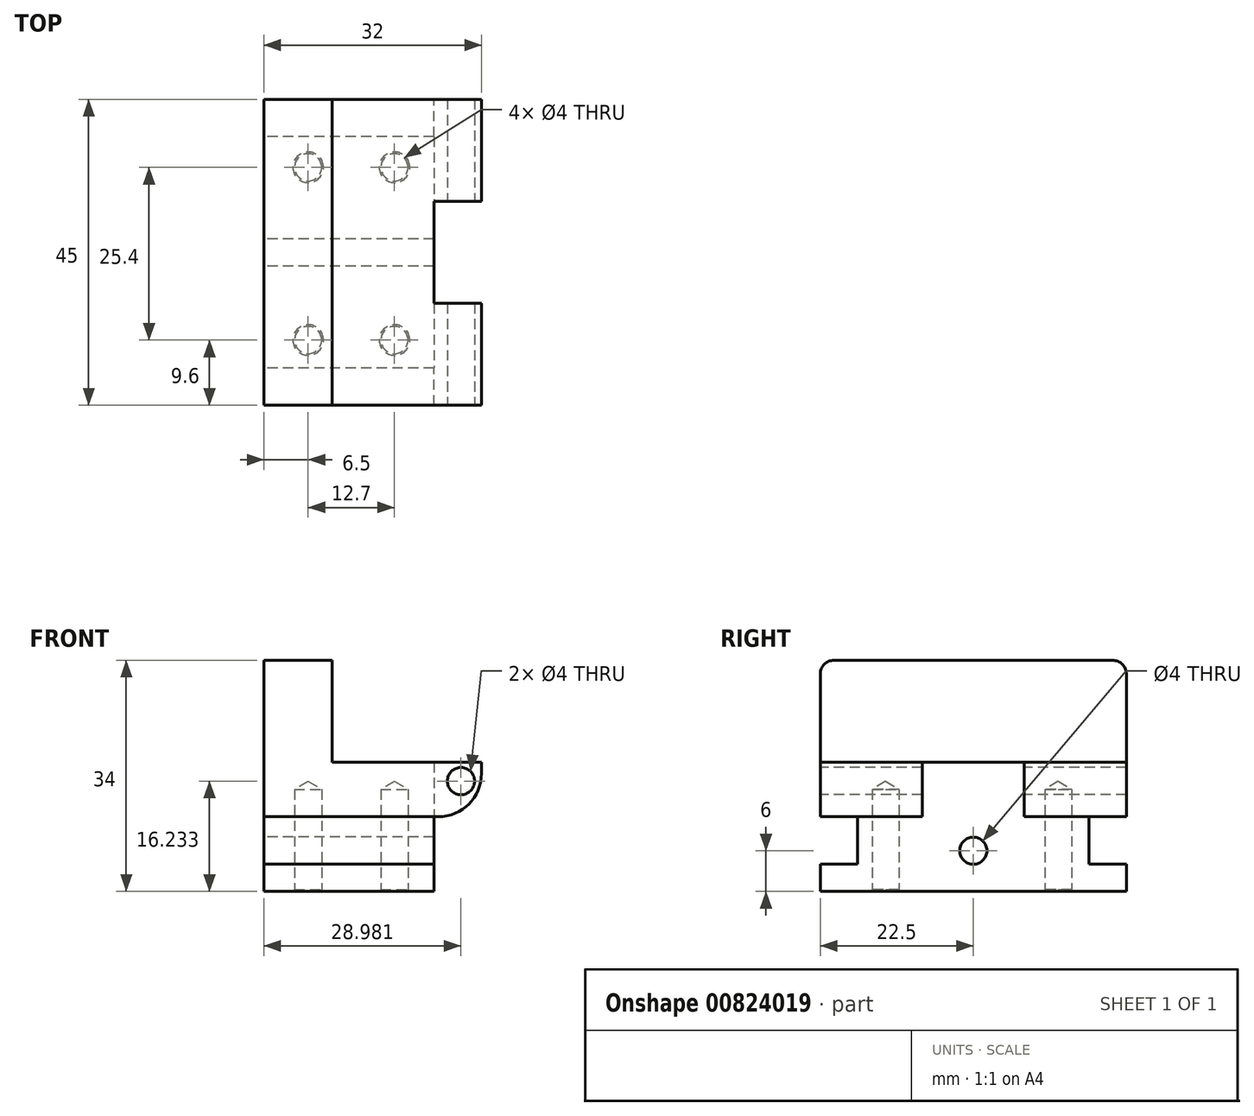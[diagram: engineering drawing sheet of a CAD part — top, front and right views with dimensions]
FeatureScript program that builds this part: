
annotation { "Feature Type Name" : "Feature", "Feature Type Description" : "" }
export const myFeature = defineFeature(function(context is Context, id is Id, definition is map)
    precondition{}
    {
        {
            var Q0;
            Q0=qCreatedBy(makeId("Right.planeOp"),FACE);
            var sketch = newSketch(context, id + "F0", { "sketchPlane" : qUnion([Q0])});
            skLineSegment(sketch, "E0.bottom", {"start": v(0, 0) * mm, "end": v(45, 0) * mm});
            skLineSegment(sketch, "E0.top", {"start": v(0, 34) * mm, "end": v(45, 34) * mm});
            skLineSegment(sketch, "E0.left", {"start": v(0, 0) * mm, "end": v(0, 4) * mm});
            skLineSegment(sketch, "E0.right", {"start": v(45, 0) * mm, "end": v(45, 4) * mm});
            skLineSegment(sketch, "E1", {"start": v(0, 4) * mm, "end": v(5.5, 4) * mm});
            skLineSegment(sketch, "E2", {"start": v(0, 11) * mm, "end": v(5.5, 11) * mm});
            skLineSegment(sketch, "E3", {"start": v(5.5, 11) * mm, "end": v(5.5, 4) * mm});
            skLineSegment(sketch, "E4", {"start": v(39.5, 11) * mm, "end": v(39.5, 4) * mm});
            skLineSegment(sketch, "E5.trimOffspring", {"start": v(39.5, 11) * mm, "end": v(45, 11) * mm});
            skLineSegment(sketch, "E6.trimOffspring", {"start": v(39.5, 4) * mm, "end": v(45, 4) * mm});
            skLineSegment(sketch, "E7.trimOffspring", {"start": v(0, 11) * mm, "end": v(0, 34) * mm});
            skLineSegment(sketch, "E8.trimOffspring", {"start": v(45, 11) * mm, "end": v(45, 34) * mm});
            skSolve(sketch);
        }
        {
            var Q0;
            Q0 = qSketchRegion(id + "F0", true);
            extrude(context, id + "F1", {"entities" : qUnion([Q0]), "depth" : 25 * mm, "offsetDistance" : 25.4 * mm});
        }
        {
            var Q0;
            Q0=makeQuery(id+"F1.opExtrude","SWEPT_FACE",FACE,{"disambiguationData":[OSD([sQuery(id+"F0.wireOp",EDGE,"E7.trimOffspring")])]});
            var sketch = newSketch(context, id + "F2", { "sketchPlane" : qUnion([Q0])});
            skLineSegment(sketch, "E9", {"start": v(10, 34) * mm, "end": v(10, 19) * mm});
            skLineSegment(sketch, "E10", {"start": v(10, 19) * mm, "end": v(25, 19) * mm});
            skLineSegment(sketch, "E11", {"start": v(25, 19) * mm, "end": v(25, 34) * mm});
            skLineSegment(sketch, "E12", {"start": v(25, 34) * mm, "end": v(10, 34) * mm});
            skSolve(sketch);
        }
        {
            var Q0;
            Q0=makeQuery(id+"F2.imprint","IMPRINT",FACE,{"disambiguationData":[TD([[makeQuery(id+"F2.imprint","IMPRINT",EDGE,{"derivedFrom":sQuery(id+"F2.wireOp",EDGE,"E9")}),1.0]])]});
            extrude(context, id + "F3", {"entities" : qUnion([Q0]), "operationType" : NewBodyOperationType.REMOVE, "endBound" : BoundingType.UP_TO_NEXT, "oppositeDirection" : true, "depth" : 25.4 * mm, "offsetDistance" : 25.4 * mm});
        }
        {
            var Q0;
            Q0=makeQuery(id+"F3.boolean.opBoolean","COPY",EDGE,{"derivedFrom":makeQuery(id+"F3.opExtrude","SWEPT_EDGE",EDGE,{"disambiguationData":[OSD([sQuery(id+"F0.wireOp",EDGE,"E0.top"),sQuery(id+"F0.wireOp",EDGE,"E7.trimOffspring"),sQuery(id+"F2.wireOp",EDGE,"E9"),sQuery(id+"F2.wireOp",EDGE,"E12")])]})});
            var Q1;
            Q1=makeQuery(id+"F1.opExtrude","SWEPT_EDGE",EDGE,{"disambiguationData":[OSD([sQuery(id+"F0.wireOp",EDGE,"E0.top"),sQuery(id+"F0.wireOp",EDGE,"E7.trimOffspring")])]});
            var Q2;
            Q2=makeQuery(id+"F1.opExtrude","SWEPT_EDGE",EDGE,{"disambiguationData":[OSD([sQuery(id+"F0.wireOp",EDGE,"E0.top"),sQuery(id+"F0.wireOp",EDGE,"E8.trimOffspring")])]});
            fillet(context, id + "F4", {"entities" : qUnion([Q0, Q1, Q2]), "radius" : 2 * mm, "tangentPropagation" : true, "allowEdgeOverflow" : false});
        }
        {
            var Q0;
            Q0=makeQuery(id+"F1.opExtrude","CAP_FACE",FACE,{"disambiguationData":[OSD([sQuery(id+"F0.wireOp",EDGE,"E0.bottom"),sQuery(id+"F0.wireOp",EDGE,"E0.top"),sQuery(id+"F0.wireOp",EDGE,"E0.left"),sQuery(id+"F0.wireOp",EDGE,"E0.right"),sQuery(id+"F0.wireOp",EDGE,"E1"),sQuery(id+"F0.wireOp",EDGE,"E2"),sQuery(id+"F0.wireOp",EDGE,"E3"),sQuery(id+"F0.wireOp",EDGE,"E4"),sQuery(id+"F0.wireOp",EDGE,"E5.trimOffspring"),sQuery(id+"F0.wireOp",EDGE,"E6.trimOffspring"),sQuery(id+"F0.wireOp",EDGE,"E7.trimOffspring"),sQuery(id+"F0.wireOp",EDGE,"E8.trimOffspring")])],"isStart":true});
            var sketch = newSketch(context, id + "F5", { "sketchPlane" : qUnion([Q0])});
            skPoint(sketch, "E13", {"position": v(-22.5, 6) * mm});
            skSolve(sketch);
        }
        {
            var Q0;
            Q0=sQuery(id+"F5.wireOp",VERTEX,"E13");
            var Q1;
            Q1=makeQuery(id+"F1.opExtrude","SWEPT_BODY",BODY,{"disambiguationData":[OSD([sQuery(id+"F0.wireOp",EDGE,"E0.bottom"),sQuery(id+"F0.wireOp",EDGE,"E0.top"),sQuery(id+"F0.wireOp",EDGE,"E0.left"),sQuery(id+"F0.wireOp",EDGE,"E0.right"),sQuery(id+"F0.wireOp",EDGE,"E1"),sQuery(id+"F0.wireOp",EDGE,"E2"),sQuery(id+"F0.wireOp",EDGE,"E3"),sQuery(id+"F0.wireOp",EDGE,"E4"),sQuery(id+"F0.wireOp",EDGE,"E5.trimOffspring"),sQuery(id+"F0.wireOp",EDGE,"E6.trimOffspring"),sQuery(id+"F0.wireOp",EDGE,"E7.trimOffspring"),sQuery(id+"F0.wireOp",EDGE,"E8.trimOffspring")])]});
            hole(context, id + "F6", {"style" : HoleStyle.SIMPLE, "endStyle" : HoleEndStyle.THROUGH, "holeDiameter" : 4 * mm, "majorDiameter" : 6.35 * mm, "isTappedThrough" : true, "tappedDepth" : 12.7 * mm, "tapClearance" : 3, "locations" : qUnion([Q0]), "scope" : qUnion([Q1])});
        }
        {
            var Q0;
            Q0=makeQuery(id+"F1.opExtrude","SWEPT_FACE",FACE,{"disambiguationData":[OSD([sQuery(id+"F0.wireOp",EDGE,"E0.bottom")])]});
            var sketch = newSketch(context, id + "F7", { "sketchPlane" : qUnion([Q0])});
            skLineSegment(sketch, "E14.bottom", {"start": v(19.2, -9.6) * mm, "end": v(6.5, -9.6) * mm});
            skLineSegment(sketch, "E14.top", {"start": v(19.2, -35) * mm, "end": v(6.5, -35) * mm});
            skLineSegment(sketch, "E14.left", {"start": v(19.2, -9.6) * mm, "end": v(19.2, -35) * mm});
            skLineSegment(sketch, "E14.right", {"start": v(6.5, -9.6) * mm, "end": v(6.5, -35) * mm});
            skSolve(sketch);
        }
        {
            var Q0;
            Q0=sQuery(id+"F7.wireOp",VERTEX,"E14.bottom.start");
            var Q1;
            Q1=sQuery(id+"F7.wireOp",VERTEX,"E14.bottom.end");
            var Q2;
            Q2=sQuery(id+"F7.wireOp",VERTEX,"E14.top.end");
            var Q3;
            Q3=sQuery(id+"F7.wireOp",VERTEX,"E14.top.start");
            var Q4;
            Q4=makeQuery(id+"F1.opExtrude","SWEPT_BODY",BODY,{"disambiguationData":[OSD([sQuery(id+"F0.wireOp",EDGE,"E0.bottom"),sQuery(id+"F0.wireOp",EDGE,"E0.top"),sQuery(id+"F0.wireOp",EDGE,"E0.left"),sQuery(id+"F0.wireOp",EDGE,"E0.right"),sQuery(id+"F0.wireOp",EDGE,"E1"),sQuery(id+"F0.wireOp",EDGE,"E2"),sQuery(id+"F0.wireOp",EDGE,"E3"),sQuery(id+"F0.wireOp",EDGE,"E4"),sQuery(id+"F0.wireOp",EDGE,"E5.trimOffspring"),sQuery(id+"F0.wireOp",EDGE,"E6.trimOffspring"),sQuery(id+"F0.wireOp",EDGE,"E7.trimOffspring"),sQuery(id+"F0.wireOp",EDGE,"E8.trimOffspring")])]});
            hole(context, id + "F8", {"style" : HoleStyle.C_SINK, "endStyle" : HoleEndStyle.BLIND, "holeDiameter" : 4 * mm, "cSinkDiameter" : 4.5 * mm, "cSinkAngle" : 90 * degree, "majorDiameter" : 6.35 * mm, "holeDepth" : 15 * mm, "isTappedThrough" : true, "tappedDepth" : 12.7 * mm, "tapClearance" : 3, "locations" : qUnion([Q0, Q1, Q2, Q3]), "scope" : qUnion([Q4])});
        }
        {
            var Q0;
            Q0=makeQuery(id+"F1.opExtrude","SWEPT_FACE",FACE,{"disambiguationData":[OSD([sQuery(id+"F0.wireOp",EDGE,"E7.trimOffspring")])]});
            var sketch = newSketch(context, id + "F9", { "sketchPlane" : qUnion([Q0])});
            skLineSegment(sketch, "E15.bottom", {"start": v(25, 19) * mm, "end": v(32, 19) * mm});
            skLineSegment(sketch, "E15.top", {"start": v(25, 11) * mm, "end": v(25.65, 11) * mm});
            skLineSegment(sketch, "E15.left", {"start": v(25, 19) * mm, "end": v(25, 11) * mm});
            skLineSegment(sketch, "E15.right", {"start": v(32, 19) * mm, "end": v(32, 17.35) * mm});
            skCircle(sketch, "E16", {"center": v(28.98, 16.23) * mm, "radius": 2 * mm});
            skPoint(sketch, "E17.visualSharp", {"position": v(32, 11) * mm});
            skArc(sketch, "E17.filletArc", {"start": v(25.65, 11) * mm, "mid": v(30.14, 12.86) * mm, "end": v(32, 17.35) * mm});
            skSolve(sketch);
        }
        {
            var Q0;
            Q0 = qSketchRegion(id + "F9", true);
            var Q1;
            Q1=makeQuery(id+"F3.boolean.opBoolean","COPY",VERTEX,{"derivedFrom":makeQuery(id+"F3.opExtrude","CAP_VERTEX",VERTEX,{"disambiguationData":[OSD([sQuery(id+"F0.wireOp",EDGE,"E7.trimOffspring"),sQuery(id+"F0.wireOp",EDGE,"E8.trimOffspring"),sQuery(id+"F2.wireOp",EDGE,"E10"),sQuery(id+"F2.wireOp",EDGE,"E11")])],"isStart":false})});
            extrude(context, id + "F10", {"entities" : qUnion([Q0]), "operationType" : NewBodyOperationType.ADD, "endBound" : BoundingType.UP_TO_VERTEX, "oppositeDirection" : true, "depth" : 15 * mm, "endBoundEntityVertex" : qUnion([Q1]), "offsetDistance" : 25.4 * mm});
        }
        {
            var Q0;
            Q0=makeQuery(id+"F1.opExtrude","SWEPT_FACE",FACE,{"disambiguationData":[OSD([sQuery(id+"F0.wireOp",EDGE,"E0.bottom")])]});
            var sketch = newSketch(context, id + "F11", { "sketchPlane" : qUnion([Q0])});
            skLineSegment(sketch, "E18.bottom", {"start": v(25, -15) * mm, "end": v(38.59, -15) * mm});
            skLineSegment(sketch, "E18.top", {"start": v(25, -30) * mm, "end": v(38.59, -30) * mm});
            skLineSegment(sketch, "E18.left", {"start": v(25, -15) * mm, "end": v(25, -30) * mm});
            skLineSegment(sketch, "E18.right", {"start": v(38.59, -15) * mm, "end": v(38.59, -30) * mm});
            skSolve(sketch);
        }
        {
            var Q0;
            Q0 = qSketchRegion(id + "F11", true);
            extrude(context, id + "F12", {"entities" : qUnion([Q0]), "operationType" : NewBodyOperationType.REMOVE, "oppositeDirection" : true, "depth" : 25.4 * mm, "offsetDistance" : 25.4 * mm});
        }
    });
